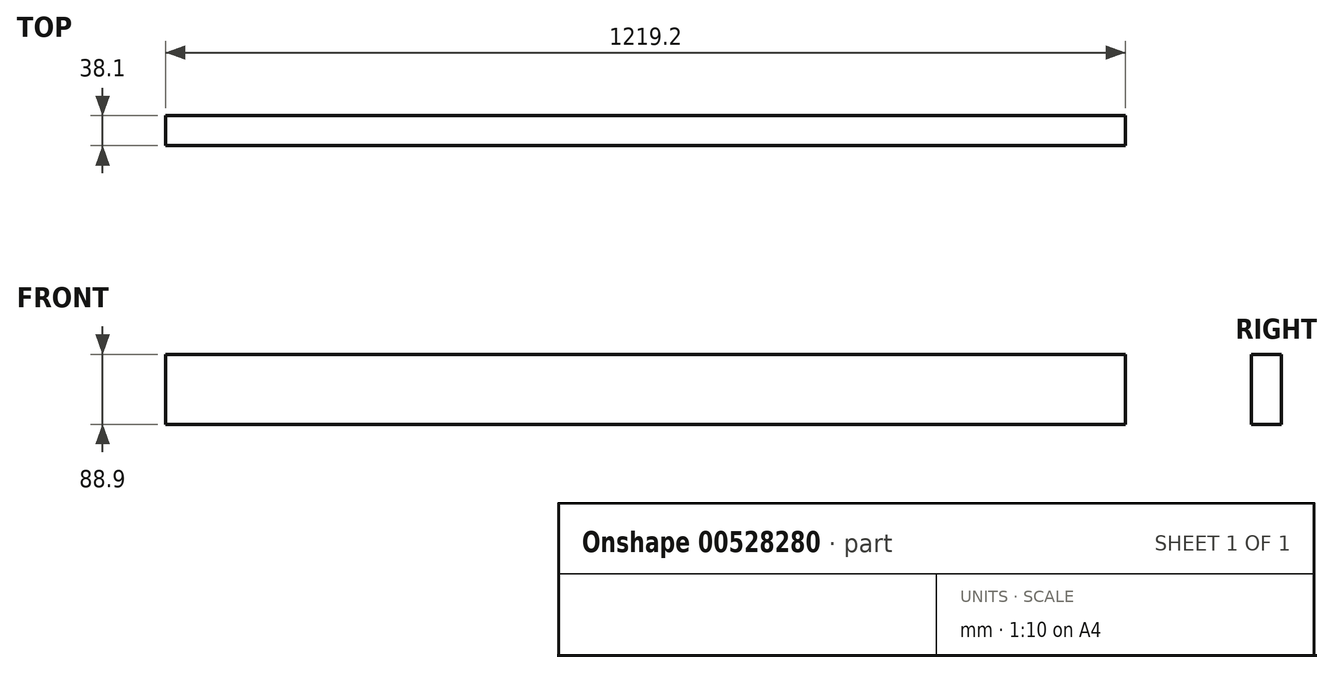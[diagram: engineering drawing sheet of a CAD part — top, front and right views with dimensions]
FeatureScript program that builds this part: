
annotation { "Feature Type Name" : "Feature", "Feature Type Description" : "" }
export const myFeature = defineFeature(function(context is Context, id is Id, definition is map)
    precondition{}
    {
        {
            var Q0;
            Q0=qCreatedBy(makeId("Top.planeOp"),FACE);
            var sketch = newSketch(context, id + "F0", { "sketchPlane" : qUnion([Q0])});
            skLineSegment(sketch, "E0.bottom", {"start": v(0, 0) * mm, "end": v(1219.2, 0) * mm});
            skLineSegment(sketch, "E0.top", {"start": v(0, 38.1) * mm, "end": v(1219.2, 38.1) * mm});
            skLineSegment(sketch, "E0.left", {"start": v(0, 0) * mm, "end": v(0, 38.1) * mm});
            skLineSegment(sketch, "E0.right", {"start": v(1219.2, 0) * mm, "end": v(1219.2, 38.1) * mm});
            skSolve(sketch);
        }
        {
            var Q0;
            Q0 = qSketchRegion(id + "F0", true);
            extrude(context, id + "F1", {"entities" : qUnion([Q0]), "depth" : 88.9 * mm, "offsetDistance" : 25.4 * mm});
        }
    });
